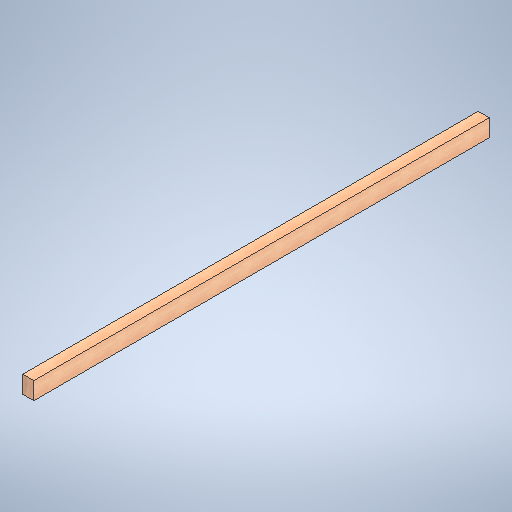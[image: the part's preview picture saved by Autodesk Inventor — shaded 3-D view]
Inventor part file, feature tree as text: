
AUTODESK INVENTOR PART (.ipt)
format: ipt  version: 2025 (Build 290162010, 162A)  size: 279,552 bytes
history: native  units: in
note: dims shown in document units (in); Inventor stores cm internally (conversion verified against a paired STEP export)
features: extrude x1, sketch x1
ambient origin geometry x8: Origin, YZ Plane, XZ Plane, XY Plane, X Axis, Y Axis, Z Axis, Center Point
bodies: Solid1 (feature_tree)
feature tree (2):
  extrude  "Extrusion1"  Depth=3.5in
  sketch  "Sketch1"  dims[d1=5.5in d2=3.5in d3=144.0in d4=0.0in]
